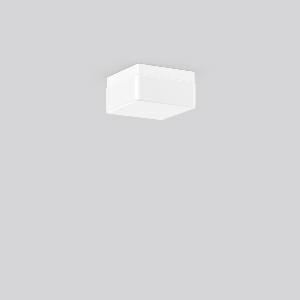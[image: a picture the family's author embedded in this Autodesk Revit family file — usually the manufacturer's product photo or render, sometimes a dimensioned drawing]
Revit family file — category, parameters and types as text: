
# Revit family: quadrat_20127_002_d047
name_source: partatom
category: Lighting Fixtures
units: mm (PartAtom-declared; Revit-internal decimal feet)

## family parameters
Cut with Voids When Loaded = No
Host = Face
Light Source = No
Part Type = Normal
Room Calculation Point = No
Round Connector Dimension = Use Diameter
Shared = No

## types (1)
- QUADRAT (1 x QA60/clear E27, 700 lm, 46 W, 3000)
    Apparent Load = 46 VA
    CIE Flux Codes = 34 63 85 72 42
    Color Rendering = 90
    Color Temperature = 3000
    Default Elevation = 1800 mm
    Description = Series: QUADRAT
Square surface-mounted luminaire in classic design. Base: plastic. Opal glass: mouth blown, silk finish. Diffuser fastening: spring system. Suitable for Ceiling mounting, Wall (surface). IP 43 ceiling mounting, IP 44 wall mounting. 
Colour: white
Length: 190 mm
Width: 190 mm
Height: 100 mm
Lamp: A60
Number of lamps: 1
Wattage: 60 W
Socket: E27
System power: 46 W
Rated luminous flux: 300 lm
Luminous efficiency: 7 lm/W
Control gear: Converter not necessary
Protection class: II
Type of protection: IP 43
    Height = 100 mm  [stored 0.328084 ft]
    Lamp = 1 x QA60/clear E27
    Lamp Light Flux = 700 lm
    Lamp Power = 46 W
    Lamp count = 1
    Length = 190 mm  [stored 0.62336 ft]
    Lifetime = 3000 h
    Luminous efficacy = 6 lm/W
    Manufacturer = RZB
    ModVariant = No
    Model = 20127.002
    Mounting Place = Ceiling, Wall
    Mounting Type = Surface mounted
    Number of Poles = 1
    OnlyDefault = Yes
    Power Factor = 1
    Product Name = QUADRAT
    Product group = Surface mounted ceiling and wall luminaires
    ProductGroupID = 305
    Protection Class = Protection class II
    Protection Degree = IP 43
    RLX_Detail_Level = 1
    RLX_Emergency_Light_Flux = 0 lm
    RLX_Emergency_Type = 0
    RLX_Emergency_Type_DB = No
    RlxData = <blob elided: 8905 chars, md5=7515a5c7>
    Socket = E27
    Standby Power = 0 W
    System Light Flux = 297 lm
    System Power = 46 W
    Type Comments = Product without accessories
    Type Image = 20127.002.jpg
    URL = http://relux.com
    VarID = ---
    Voltage = 230 V
    Voltage Range = 220-240 V
    Weight = 0.00 kg
    Width = 190 mm  [stored 0.62336 ft]

note: [stored X ft] marks values corroborated as IEEE doubles in the binary element streams (Revit-internal decimal feet)

## geometry (parser evidence)
native form markers: Sweep x11
no freeform markers — native parametric forms only
